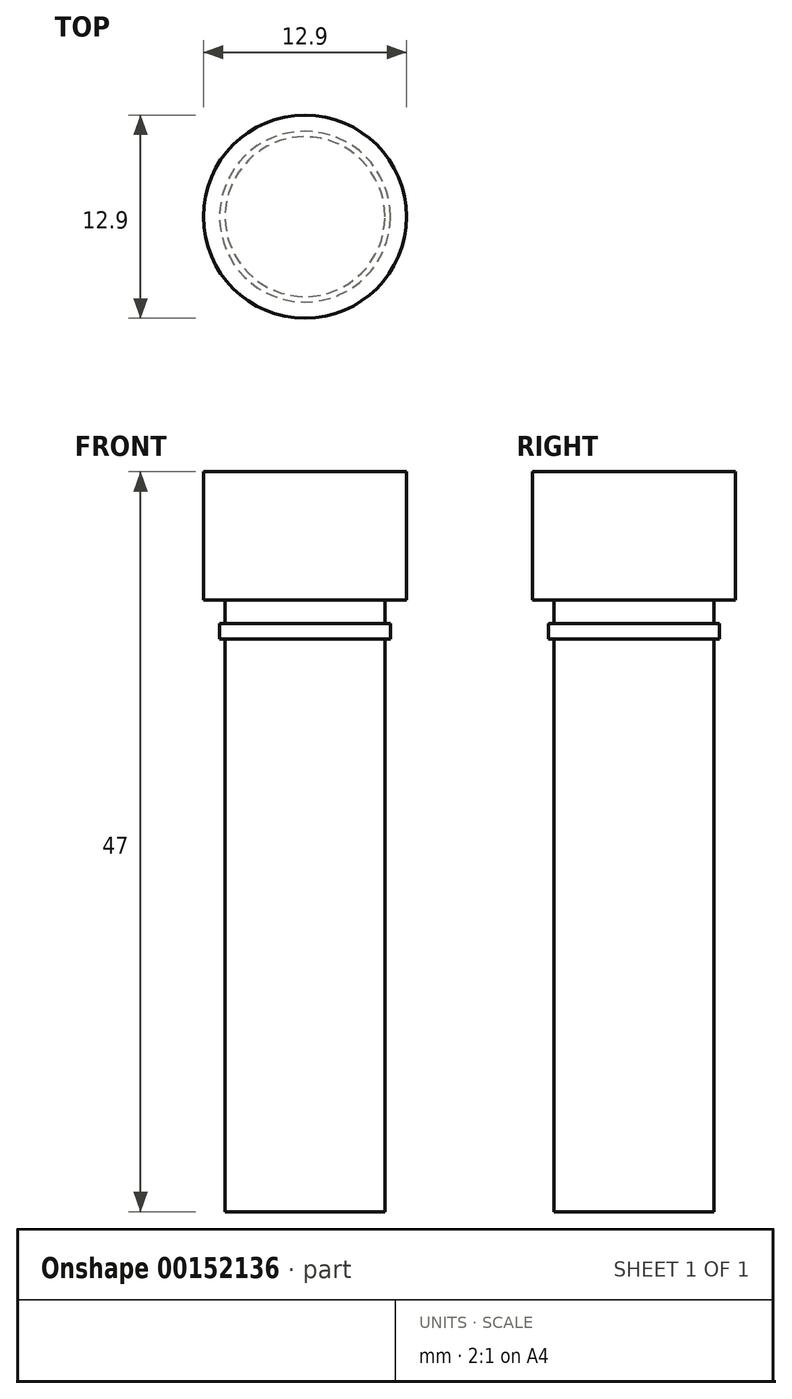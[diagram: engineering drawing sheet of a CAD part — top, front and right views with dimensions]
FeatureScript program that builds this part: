
annotation { "Feature Type Name" : "Feature", "Feature Type Description" : "" }
export const myFeature = defineFeature(function(context is Context, id is Id, definition is map)
    precondition{}
    {
        {
            var Q0;
            Q0=qCreatedBy(makeId("Front.planeOp"),FACE);
            var sketch = newSketch(context, id + "F0", { "sketchPlane" : qUnion([Q0])});
            skLineSegment(sketch, "E0", {"start": v(0, 0) * mm, "end": v(0, 47) * mm});
            skLineSegment(sketch, "E1", {"start": v(5.08, 0) * mm, "end": v(5.08, 36.37) * mm});
            skLineSegment(sketch, "E2", {"start": v(5.08, 0) * mm, "end": v(0, 0) * mm});
            skLineSegment(sketch, "E3", {"start": v(5.08, 36.37) * mm, "end": v(5.42, 36.37) * mm});
            skLineSegment(sketch, "E4", {"start": v(5.42, 36.37) * mm, "end": v(5.42, 37.37) * mm});
            skLineSegment(sketch, "E5", {"start": v(5.42, 37.37) * mm, "end": v(5.08, 37.37) * mm});
            skLineSegment(sketch, "E6", {"start": v(5.08, 37.37) * mm, "end": v(5.08, 38.84) * mm});
            skLineSegment(sketch, "E7", {"start": v(5.08, 38.84) * mm, "end": v(6.45, 38.84) * mm});
            skLineSegment(sketch, "E8", {"start": v(6.45, 38.84) * mm, "end": v(6.45, 47) * mm});
            skLineSegment(sketch, "E9", {"start": v(6.45, 47) * mm, "end": v(0, 47) * mm});
            skSolve(sketch);
        }
        {
            var Q0;
            Q0=makeQuery(id+"F0.imprint","IMPRINT",FACE,{"disambiguationData":[TD([[makeQuery(id+"F0.imprint","IMPRINT",EDGE,{"derivedFrom":sQuery(id+"F0.wireOp",EDGE,"E0")}),-1.0]])]});
            var Q1;
            Q1 = qConstructionFilter(qBodyType(qCreatedBy(id + "F0" ,EDGE), BodyType.WIRE), ConstructionObject.NO);
            var Q2;
            Q2=sQuery(id+"F0.wireOp",EDGE,"E0");
            revolve(context, id + "F1", {"entities" : qUnion([Q0]), "surfaceEntities" : qUnion([Q1]), "axis" : qUnion([Q2]), "revolveType" : RevolveType.FULL});
        }
    });
